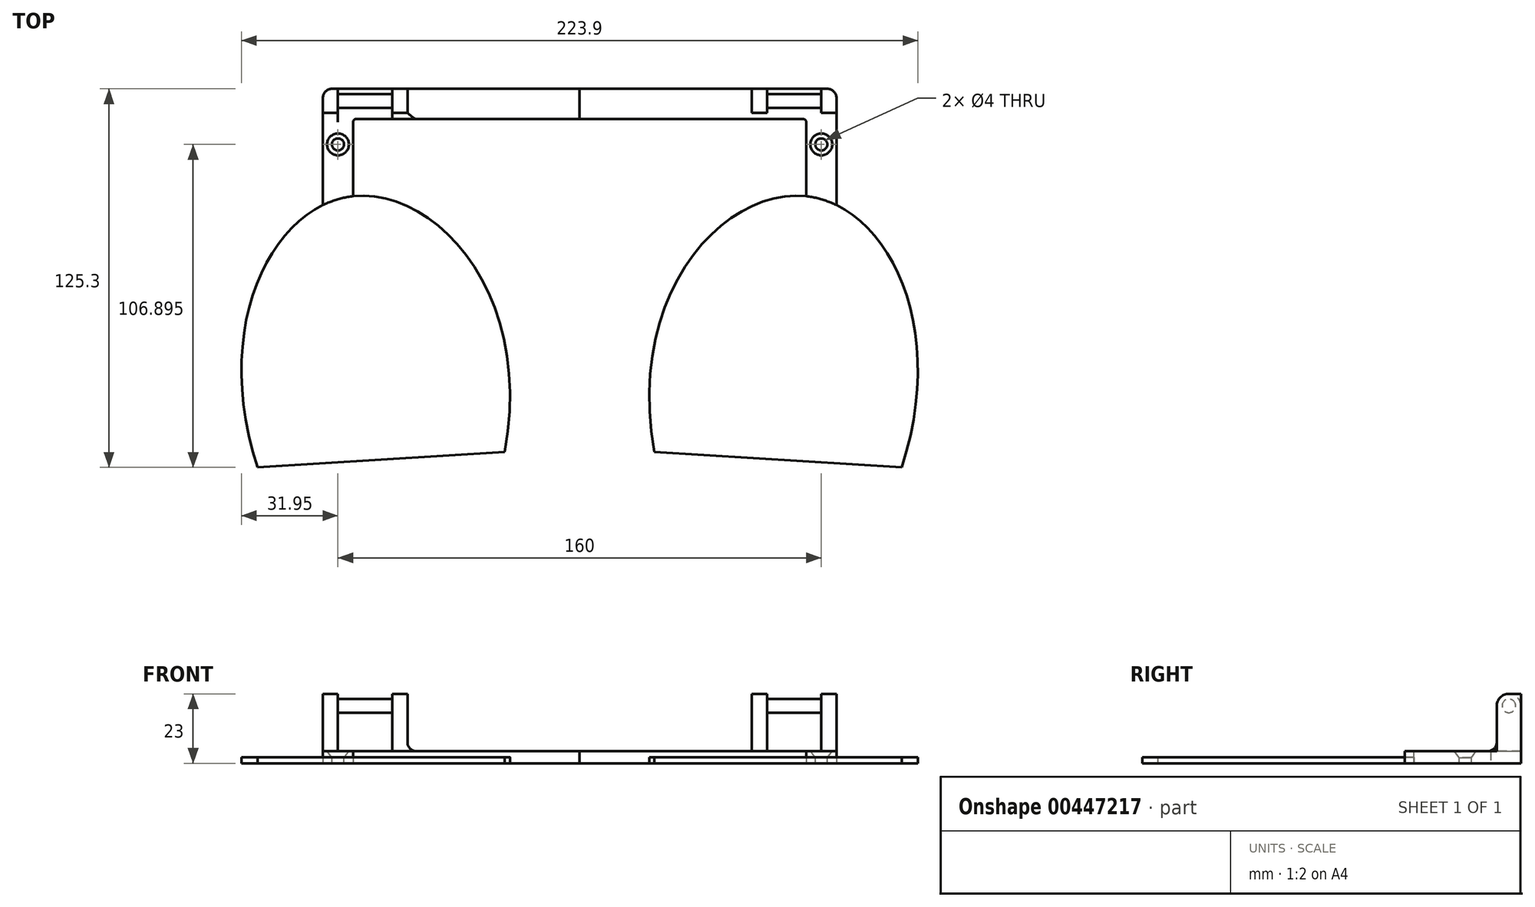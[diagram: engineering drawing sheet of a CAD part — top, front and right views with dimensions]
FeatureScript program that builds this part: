
annotation { "Feature Type Name" : "Feature", "Feature Type Description" : "" }
export const myFeature = defineFeature(function(context is Context, id is Id, definition is map)
    precondition{}
    {
        {
            var Q0;
            Q0=qCreatedBy(makeId("Top.planeOp"),FACE);
            var sketch = newSketch(context, id + "F0", { "sketchPlane" : qUnion([Q0])});
            skLineSegment(sketch, "E0.bottom", {"start": v(-85, 0) * mm, "end": v(-75, 0) * mm});
            skLineSegment(sketch, "E0.top", {"start": v(-85, 40) * mm, "end": v(0, 40) * mm});
            skLineSegment(sketch, "E0.left", {"start": v(-85, 0) * mm, "end": v(-85, 40) * mm});
            skLineSegment(sketch, "E1.top", {"start": v(-75, 30) * mm, "end": v(0, 30) * mm});
            skLineSegment(sketch, "E1.left", {"start": v(-75, 0) * mm, "end": v(-75, 30) * mm});
            skLineSegment(sketch, "E2", {"start": v(-106.6, -85.3) * mm, "end": v(-24.75, -80.2) * mm});
            skFitSpline(sketch, "E3", {"points": [v(-106.6, -85.3) * mm, v(-75.38, 4.38) * mm, v(-24.75, -80.2) * mm], "startDerivative": vector(-93.46, 284.06) * mm, "endDerivative": vector(-56.97, -317) * mm});
            skLineSegment(sketch, "E4", {"start": v(0, 40) * mm, "end": v(0, 30) * mm});
            skSolve(sketch);
        }
        {
            var Q0;
            {var subQ6=sQuery(id+"F0.wireOp",EDGE,"E0.top");Q0=makeQuery(id+"F0.imprint","IMPRINT",FACE,{"disambiguationData":[TD([[makeQuery(id+"F0.imprint","IMPRINT",EDGE,{"derivedFrom":subQ6}),-1.0]])]});}
            extrude(context, id + "F1", {"entities" : qUnion([Q0]), "depth" : 4 * mm, "offsetDistance" : 25 * mm});
        }
        {
            var Q0;
            {var subQ8=sQuery(id+"F0.wireOp",EDGE,"E2");Q0=makeQuery(id+"F0.imprint","IMPRINT",FACE,{"disambiguationData":[TD([[makeQuery(id+"F0.imprint","IMPRINT",EDGE,{"derivedFrom":subQ8}),1.0]])]});}
            var Q1;
            {var subQ5=sQuery(id+"F0.wireOp",EDGE,"79211e8e-8244-4d67-8351-19a3457fbf290.MirrorCS");Q1=makeQuery(id+"F0.imprint","IMPRINT",FACE,{"disambiguationData":[TD([[makeQuery(id+"F0.imprint","IMPRINT",EDGE,{"derivedFrom":subQ5}),-1.0]])]});}
            var Q2;
            {var subQ0=sQuery(id+"F0.wireOp",EDGE,"E0.right");var subQ1=sQuery(id+"F0.wireOp",EDGE,"E0.bottom");var subQ2=makeQuery(id+"F0.imprint","INTERSECT",VERTEX,{"derivedFrom":[subQ1,subQ0]});Q2=makeQuery(id+"F0.imprint","IMPRINT",FACE,{"disambiguationData":[TD([[makeQuery(id+"F0.imprint","IMPRINT",EDGE,{"disambiguationData":[TD([[subQ2,-1.0]])],"derivedFrom":subQ0}),1.0]])]});}
            var Q3;
            {var subQ1=sQuery(id+"F0.wireOp",EDGE,"E1.bottom");var subQ3=sQuery(id+"F0.wireOp",EDGE,"5d9b1bdb-1e1e-4ad1-b13f-3cf6168354ab0.MirrorCS");var subQ4=makeQuery(id+"F0.imprint","INTERSECT",VERTEX,{"derivedFrom":[subQ1,subQ3]});Q3=makeQuery(id+"F0.imprint","IMPRINT",FACE,{"disambiguationData":[TD([[makeQuery(id+"F0.imprint","IMPRINT",EDGE,{"disambiguationData":[TD([[subQ4,1.0]])],"derivedFrom":subQ3}),1.0]])]});}
            var Q4;
            {var subQ0=sQuery(id+"F0.wireOp",EDGE,"E0.left");var subQ1=sQuery(id+"F0.wireOp",EDGE,"E0.bottom");var subQ2=makeQuery(id+"F0.imprint","INTERSECT",VERTEX,{"derivedFrom":[subQ1,subQ0]});Q4=makeQuery(id+"F0.imprint","IMPRINT",FACE,{"disambiguationData":[TD([[makeQuery(id+"F0.imprint","IMPRINT",EDGE,{"disambiguationData":[TD([[subQ2,-1.0]])],"derivedFrom":subQ0}),-1.0]])]});}
            var Q5;
            {var subQ1=sQuery(id+"F0.wireOp",EDGE,"E1.bottom");var subQ3=sQuery(id+"F0.wireOp",EDGE,"E3");var subQ4=makeQuery(id+"F0.imprint","INTERSECT",VERTEX,{"derivedFrom":[subQ1,subQ3]});Q5=makeQuery(id+"F0.imprint","IMPRINT",FACE,{"disambiguationData":[TD([[makeQuery(id+"F0.imprint","IMPRINT",EDGE,{"disambiguationData":[TD([[subQ4,1.0]])],"derivedFrom":subQ3}),-1.0]])]});}
            extrude(context, id + "F2", {"entities" : qUnion([Q0, Q1, Q2, Q3, Q4, Q5]), "operationType" : NewBodyOperationType.ADD, "depth" : 2 * mm, "offsetDistance" : 25 * mm});
        }
        {
            var Q0;
            Q0=qCreatedBy(makeId("Right.planeOp"),FACE);
            var Q1;
            Q1=sQuery(id+"F0.wireOp",VERTEX,"E0.left.end");
            cPlane(context, id + "F3", {"entities" : qUnion([Q0, Q1]), "cplaneType" : CPlaneType.PLANE_POINT, "offset" : 25 * mm, "width" : 150 * mm, "height" : 150 * mm});
        }
        {
            var Q0;
            Q0=qCreatedBy(id+"F3.planeOp",FACE);
            var sketch = newSketch(context, id + "F4", { "sketchPlane" : qUnion([Q0])});
            skCircle(sketch, "E5", {"center": v(36, 19) * mm, "radius": 2.25 * mm});
            skLineSegment(sketch, "E6.bottom", {"start": v(32, 23) * mm, "end": v(40, 23) * mm});
            skLineSegment(sketch, "E6.top", {"start": v(32, 0) * mm, "end": v(40, 0) * mm});
            skLineSegment(sketch, "E6.left", {"start": v(32, 23) * mm, "end": v(32, 0) * mm});
            skLineSegment(sketch, "E6.right", {"start": v(40, 23) * mm, "end": v(40, 0) * mm});
            skSolve(sketch);
        }
        {
            var Q0;
            Q0=qCreatedBy(id+"F3.planeOp",FACE);
            cPlane(context, id + "F5", {"entities" : qUnion([Q0]), "cplaneType" : CPlaneType.OFFSET, "offset" : 28 * mm, "width" : 150 * mm, "height" : 150 * mm});
        }
        {
            var Q0;
            Q0=makeQuery(id+"F4.imprint","IMPRINT",FACE,{"disambiguationData":[TD([[makeQuery(id+"F4.imprint","IMPRINT",EDGE,{"derivedFrom":sQuery(id+"F4.wireOp",EDGE,"E5")}),-1.0]])]});
            var Q1;
            Q1=makeQuery(id+"F4.imprint","IMPRINT",FACE,{"disambiguationData":[TD([[makeQuery(id+"F4.imprint","IMPRINT",EDGE,{"derivedFrom":sQuery(id+"F4.wireOp",EDGE,"E5")}),1.0]])]});
            extrude(context, id + "F6", {"entities" : qUnion([Q0, Q1]), "operationType" : NewBodyOperationType.ADD, "depth" : 5 * mm, "offsetDistance" : 25 * mm});
        }
        {
            var Q0;
            Q0=qCreatedBy(id+"F5.planeOp",FACE);
            var sketch = newSketch(context, id + "F7", { "sketchPlane" : qUnion([Q0])});
            skLineSegment(sketch, "E7.bottom", {"start": v(40, 0) * mm, "end": v(32, 0) * mm});
            skLineSegment(sketch, "E7.top", {"start": v(40, 23) * mm, "end": v(32, 23) * mm});
            skLineSegment(sketch, "E7.left", {"start": v(40, 0) * mm, "end": v(40, 23) * mm});
            skLineSegment(sketch, "E7.right", {"start": v(32, 0) * mm, "end": v(32, 23) * mm});
            skSolve(sketch);
        }
        {
            var Q0;
            Q0=makeQuery(id+"F7.imprint","IMPRINT",FACE,{"disambiguationData":[TD([[makeQuery(id+"F7.imprint","IMPRINT",EDGE,{"derivedFrom":sQuery(id+"F7.wireOp",EDGE,"E7.bottom")}),-1.0]])]});
            extrude(context, id + "F8", {"entities" : qUnion([Q0]), "operationType" : NewBodyOperationType.ADD, "oppositeDirection" : true, "depth" : 5 * mm, "offsetDistance" : 25 * mm});
        }
        {
            var Q0;
            Q0=makeQuery(id+"F4.imprint","IMPRINT",FACE,{"disambiguationData":[TD([[makeQuery(id+"F4.imprint","IMPRINT",EDGE,{"derivedFrom":sQuery(id+"F4.wireOp",EDGE,"E5")}),1.0]])]});
            var Q1;
            Q1=makeQuery(id+"F8.opExtrude","CAP_FACE",FACE,{"disambiguationData":[OSD([sQuery(id+"F7.wireOp",EDGE,"E7.bottom"),sQuery(id+"F7.wireOp",EDGE,"E7.top"),sQuery(id+"F7.wireOp",EDGE,"E7.left"),sQuery(id+"F7.wireOp",EDGE,"E7.right")])],"isStart":false});
            extrude(context, id + "F9", {"entities" : qUnion([Q0]), "operationType" : NewBodyOperationType.ADD, "endBound" : BoundingType.UP_TO_SURFACE, "depth" : 32 * mm, "endBoundEntityFace" : qUnion([Q1]), "offsetDistance" : 25 * mm});
        }
        {
            var Q0;
            Q0=makeQuery(id+"F1.opExtrude","SWEPT_EDGE",EDGE,{"disambiguationData":[OSD([sQuery(id+"F0.wireOp",EDGE,"E0.top"),sQuery(id+"F0.wireOp",EDGE,"E0.left")])]});
            fillet(context, id + "F10", {"entities" : qUnion([Q0]), "radius" : 3 * mm, "tangentPropagation" : true, "allowEdgeOverflow" : false});
        }
        {
            var Q0;
            Q0=makeQuery(id+"F1.opExtrude","SWEPT_EDGE",EDGE,{"disambiguationData":[OSD([sQuery(id+"F0.wireOp",EDGE,"E1.top"),sQuery(id+"F0.wireOp",EDGE,"E1.left")])]});
            fillet(context, id + "F11", {"entities" : qUnion([Q0]), "radius" : 1 * mm, "tangentPropagation" : true, "allowEdgeOverflow" : false});
        }
        {
            var Q0;
            Q0=makeQuery(id+"F8.opExtrude","SWEPT_EDGE",EDGE,{"disambiguationData":[OSD([sQuery(id+"F7.wireOp",EDGE,"E7.top"),sQuery(id+"F7.wireOp",EDGE,"E7.right")])]});
            var Q1;
            Q1=makeQuery(id+"F8.opExtrude","SWEPT_EDGE",EDGE,{"disambiguationData":[OSD([sQuery(id+"F7.wireOp",EDGE,"E7.top"),sQuery(id+"F7.wireOp",EDGE,"E7.left")])]});
            var Q2;
            Q2=makeQuery(id+"F6.opExtrude","SWEPT_EDGE",EDGE,{"disambiguationData":[OSD([sQuery(id+"F4.wireOp",EDGE,"E6.bottom"),sQuery(id+"F4.wireOp",EDGE,"E6.left")])]});
            fillet(context, id + "F12", {"entities" : qUnion([Q0, Q1, Q2]), "radius" : 4 * mm, "tangentPropagation" : true, "allowEdgeOverflow" : false});
        }
        {
            var Q0;
            Q0=qCreatedBy(makeId("Top.planeOp"),FACE);
            cPlane(context, id + "F13", {"entities" : qUnion([Q0]), "cplaneType" : CPlaneType.OFFSET, "offset" : 7 * mm, "width" : 150 * mm, "height" : 150 * mm});
        }
        {
            var Q0;
            Q0=qCreatedBy(id+"F13.planeOp",FACE);
            var sketch = newSketch(context, id + "F14", { "sketchPlane" : qUnion([Q0])});
            skPoint(sketch, "E8", {"position": v(-80, 21.6) * mm});
            skSolve(sketch);
        }
        {
            var Q0;
            Q0=sQuery(id+"F14.wireOp",VERTEX,"E8");
            var Q1;
            Q1=makeQuery(id+"F1.opExtrude","SWEPT_BODY",BODY,{"disambiguationData":[OSD([sQuery(id+"F0.wireOp",EDGE,"E0.top"),sQuery(id+"F0.wireOp",EDGE,"E0.left"),sQuery(id+"F0.wireOp",EDGE,"E0.right"),sQuery(id+"F0.wireOp",EDGE,"E1.top"),sQuery(id+"F0.wireOp",EDGE,"E1.left"),sQuery(id+"F0.wireOp",EDGE,"E1.right"),sQuery(id+"F0.wireOp",EDGE,"E3"),sQuery(id+"F0.wireOp",EDGE,"5d9b1bdb-1e1e-4ad1-b13f-3cf6168354ab0.MirrorCS")])]});
            var Q2;
            Q2=makeQuery(id+"F16.opPattern","COPY",BODY,{"derivedFrom":makeQuery(id+"F1.opExtrude","SWEPT_BODY",BODY,{"disambiguationData":[OSD([sQuery(id+"F0.wireOp",EDGE,"E0.top"),sQuery(id+"F0.wireOp",EDGE,"E0.left"),sQuery(id+"F0.wireOp",EDGE,"E0.right"),sQuery(id+"F0.wireOp",EDGE,"E1.top"),sQuery(id+"F0.wireOp",EDGE,"E1.left"),sQuery(id+"F0.wireOp",EDGE,"E1.right"),sQuery(id+"F0.wireOp",EDGE,"E3"),sQuery(id+"F0.wireOp",EDGE,"5d9b1bdb-1e1e-4ad1-b13f-3cf6168354ab0.MirrorCS")])]}),"instanceName":"1"});
            hole(context, id + "F15", {"style" : HoleStyle.C_SINK, "endStyle" : HoleEndStyle.THROUGH, "holeDiameter" : 4 * mm, "cSinkDiameter" : 7.25 * mm, "cSinkAngle" : 75 * degree, "majorDiameter" : 5 * mm, "isTappedThrough" : true, "tappedDepth" : 12 * mm, "tapClearance" : 3, "locations" : qUnion([Q0]), "scope" : qUnion([Q1, Q2])});
        }
        {
            var Q0;
            Q0=makeQuery(id+"F1.opExtrude","SWEPT_BODY",BODY,{"disambiguationData":[OSD([sQuery(id+"F0.wireOp",EDGE,"E0.top"),sQuery(id+"F0.wireOp",EDGE,"E0.left"),sQuery(id+"F0.wireOp",EDGE,"E0.right"),sQuery(id+"F0.wireOp",EDGE,"E1.top"),sQuery(id+"F0.wireOp",EDGE,"E1.left"),sQuery(id+"F0.wireOp",EDGE,"E1.right"),sQuery(id+"F0.wireOp",EDGE,"E3"),sQuery(id+"F0.wireOp",EDGE,"5d9b1bdb-1e1e-4ad1-b13f-3cf6168354ab0.MirrorCS")])]});
            var Q1;
            Q1=qCreatedBy(makeId("Right.planeOp"),FACE);
            mirror(context, id + "F16", {"entities" : qUnion([Q0]), "mirrorPlane" : qUnion([Q1])});
        }
        {
            var Q0;
            Q0=makeQuery(id+"F8.boolean.opBoolean","INTERSECT",EDGE,{"derivedFrom":[makeQuery(id+"F1.opExtrude","CAP_FACE",FACE,{"disambiguationData":[OSD([sQuery(id+"F0.wireOp",EDGE,"E0.top"),sQuery(id+"F0.wireOp",EDGE,"E0.left"),sQuery(id+"F0.wireOp",EDGE,"E1.top"),sQuery(id+"F0.wireOp",EDGE,"E1.left"),sQuery(id+"F0.wireOp",EDGE,"E3"),sQuery(id+"F0.wireOp",EDGE,"E4")])],"isStart":false}),makeQuery(id+"F8.opExtrude","CAP_FACE",FACE,{"disambiguationData":[OSD([sQuery(id+"F7.wireOp",EDGE,"E7.bottom"),sQuery(id+"F7.wireOp",EDGE,"E7.top"),sQuery(id+"F7.wireOp",EDGE,"E7.left"),sQuery(id+"F7.wireOp",EDGE,"E7.right")])],"isStart":true})]});
            var Q1;
            Q1=makeQuery(id+"F8.boolean.opBoolean","INTERSECT",EDGE,{"derivedFrom":[makeQuery(id+"F1.opExtrude","CAP_FACE",FACE,{"disambiguationData":[OSD([sQuery(id+"F0.wireOp",EDGE,"E0.top"),sQuery(id+"F0.wireOp",EDGE,"E0.left"),sQuery(id+"F0.wireOp",EDGE,"E1.top"),sQuery(id+"F0.wireOp",EDGE,"E1.left"),sQuery(id+"F0.wireOp",EDGE,"E3"),sQuery(id+"F0.wireOp",EDGE,"E4")])],"isStart":false}),makeQuery(id+"F8.opExtrude","SWEPT_FACE",FACE,{"disambiguationData":[OSD([sQuery(id+"F7.wireOp",EDGE,"E7.right")])]})]});
            var Q2;
            Q2=makeQuery(id+"F6.boolean.opBoolean","INTERSECT",EDGE,{"derivedFrom":[makeQuery(id+"F1.opExtrude","CAP_FACE",FACE,{"disambiguationData":[OSD([sQuery(id+"F0.wireOp",EDGE,"E0.top"),sQuery(id+"F0.wireOp",EDGE,"E0.left"),sQuery(id+"F0.wireOp",EDGE,"E1.top"),sQuery(id+"F0.wireOp",EDGE,"E1.left"),sQuery(id+"F0.wireOp",EDGE,"E3"),sQuery(id+"F0.wireOp",EDGE,"E4")])],"isStart":false}),makeQuery(id+"F6.opExtrude","SWEPT_FACE",FACE,{"disambiguationData":[OSD([sQuery(id+"F4.wireOp",EDGE,"E6.left")])]})]});
            fillet(context, id + "F17", {"entities" : qUnion([Q0, Q1, Q2]), "radius" : 3 * mm, "tangentPropagation" : true, "allowEdgeOverflow" : false});
        }
    });
